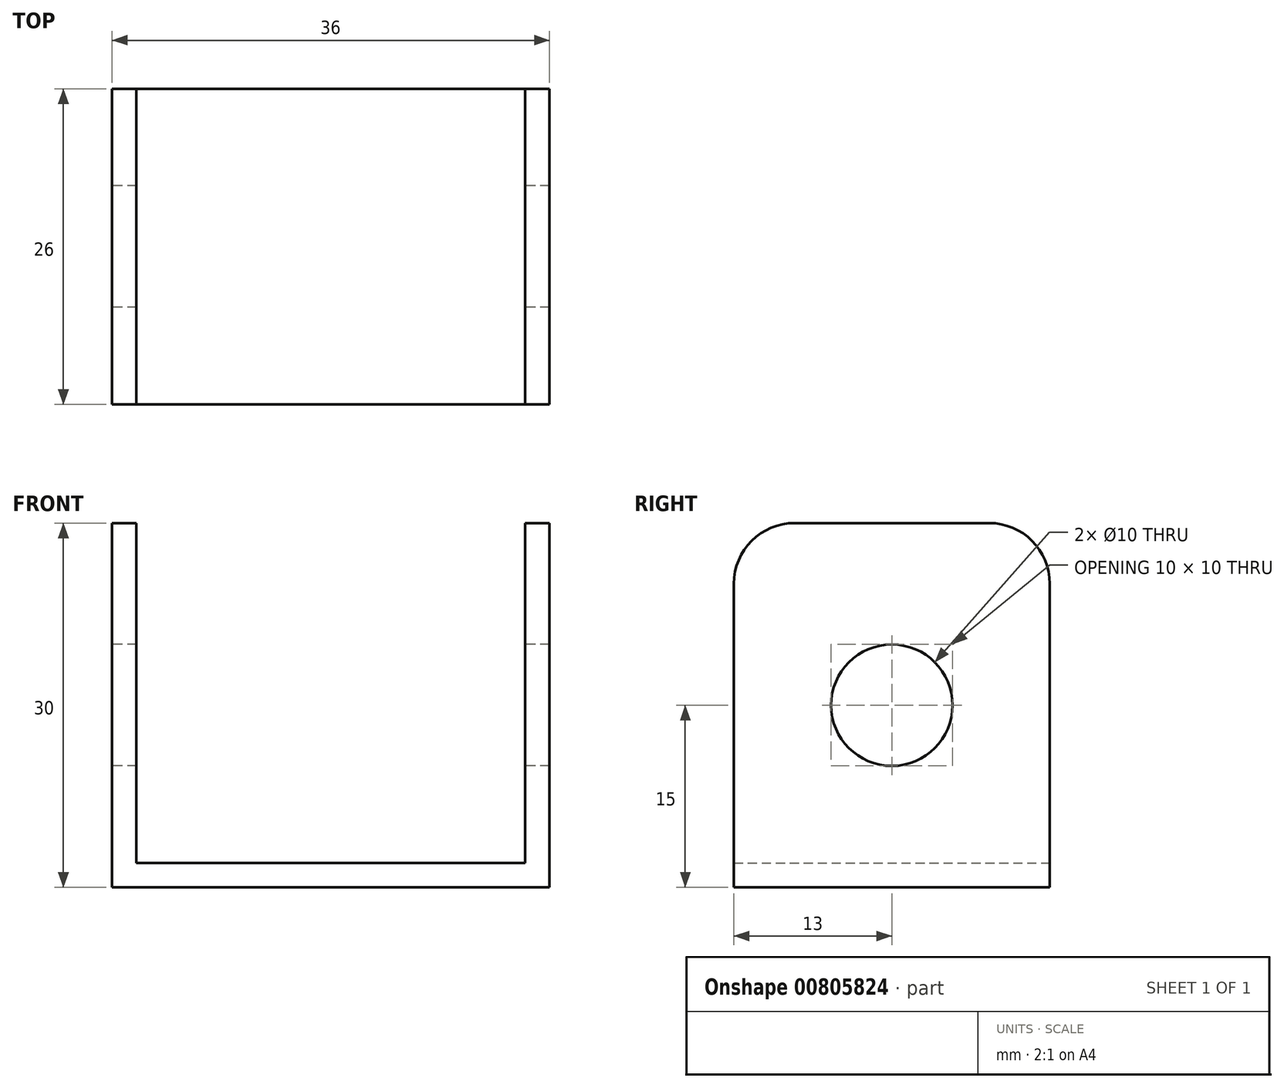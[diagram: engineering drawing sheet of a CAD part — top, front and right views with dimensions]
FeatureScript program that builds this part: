
annotation { "Feature Type Name" : "Feature", "Feature Type Description" : "" }
export const myFeature = defineFeature(function(context is Context, id is Id, definition is map)
    precondition{}
    {
        {
            var Q0;
            Q0=qCreatedBy(makeId("Front.planeOp"),FACE);
            var sketch = newSketch(context, id + "F0", { "sketchPlane" : qUnion([Q0])});
            skLineSegment(sketch, "E0.bottom", {"start": v(-18, 15) * mm, "end": v(-16, 15) * mm});
            skLineSegment(sketch, "E0.top", {"start": v(-18, -15) * mm, "end": v(18, -15) * mm});
            skLineSegment(sketch, "E0.left", {"start": v(-18, 15) * mm, "end": v(-18, -15) * mm});
            skLineSegment(sketch, "E0.right", {"start": v(18, 15) * mm, "end": v(18, -15) * mm});
            skPoint(sketch, "E0.middle", {"position": v(0, 0) * mm});
            skLineSegment(sketch, "E1.top", {"start": v(-16, -13) * mm, "end": v(16, -13) * mm});
            skLineSegment(sketch, "E1.left", {"start": v(-16, 13) * mm, "end": v(-16, -13) * mm});
            skLineSegment(sketch, "E1.right", {"start": v(16, 13) * mm, "end": v(16, -13) * mm});
            skLineSegment(sketch, "E2", {"start": v(-16, 13) * mm, "end": v(-16, 15) * mm});
            skLineSegment(sketch, "E3", {"start": v(16, 13) * mm, "end": v(16, 15) * mm});
            skLineSegment(sketch, "E4.trimOffspring", {"start": v(16, 15) * mm, "end": v(18, 15) * mm});
            skSolve(sketch);
        }
        {
            var Q0;
            Q0 = qSketchRegion(id + "F0", true);
            extrude(context, id + "F1", {"entities" : qUnion([Q0]), "depth" : 26 * mm, "offsetDistance" : 25 * mm});
        }
        {
            var Q0;
            Q0=makeQuery(id+"F1.opExtrude","SWEPT_FACE",FACE,{"disambiguationData":[OSD([sQuery(id+"F0.wireOp",EDGE,"E0.left")])]});
            var sketch = newSketch(context, id + "F2", { "sketchPlane" : qUnion([Q0])});
            skCircle(sketch, "E5", {"center": v(13, 0) * mm, "radius": 5 * mm});
            skPoint(sketch, "E5.centerSnap0", {"position": v(13, 15) * mm});
            skSolve(sketch);
        }
        {
            var Q0;
            Q0 = qSketchRegion(id + "F2", true);
            extrude(context, id + "F3", {"entities" : qUnion([Q0]), "operationType" : NewBodyOperationType.REMOVE, "endBound" : BoundingType.THROUGH_ALL, "oppositeDirection" : true, "depth" : 25 * mm, "offsetDistance" : 25 * mm});
        }
        {
            var Q0;
            Q0=makeQuery(id+"F1.opExtrude","CAP_EDGE",EDGE,{"disambiguationData":[OSD([sQuery(id+"F0.wireOp",EDGE,"E0.bottom")])],"isStart":true});
            var Q1;
            Q1=makeQuery(id+"F1.opExtrude","CAP_EDGE",EDGE,{"disambiguationData":[OSD([sQuery(id+"F0.wireOp",EDGE,"E0.bottom")])],"isStart":false});
            var Q2;
            Q2=makeQuery(id+"F1.opExtrude","CAP_EDGE",EDGE,{"disambiguationData":[OSD([sQuery(id+"F0.wireOp",EDGE,"E4.trimOffspring")])],"isStart":false});
            var Q3;
            Q3=makeQuery(id+"F1.opExtrude","CAP_EDGE",EDGE,{"disambiguationData":[OSD([sQuery(id+"F0.wireOp",EDGE,"E4.trimOffspring")])],"isStart":true});
            fillet(context, id + "F4", {"entities" : qUnion([Q0, Q1, Q2, Q3]), "radius" : 5 * mm, "tangentPropagation" : true, "allowEdgeOverflow" : false});
        }
    });
